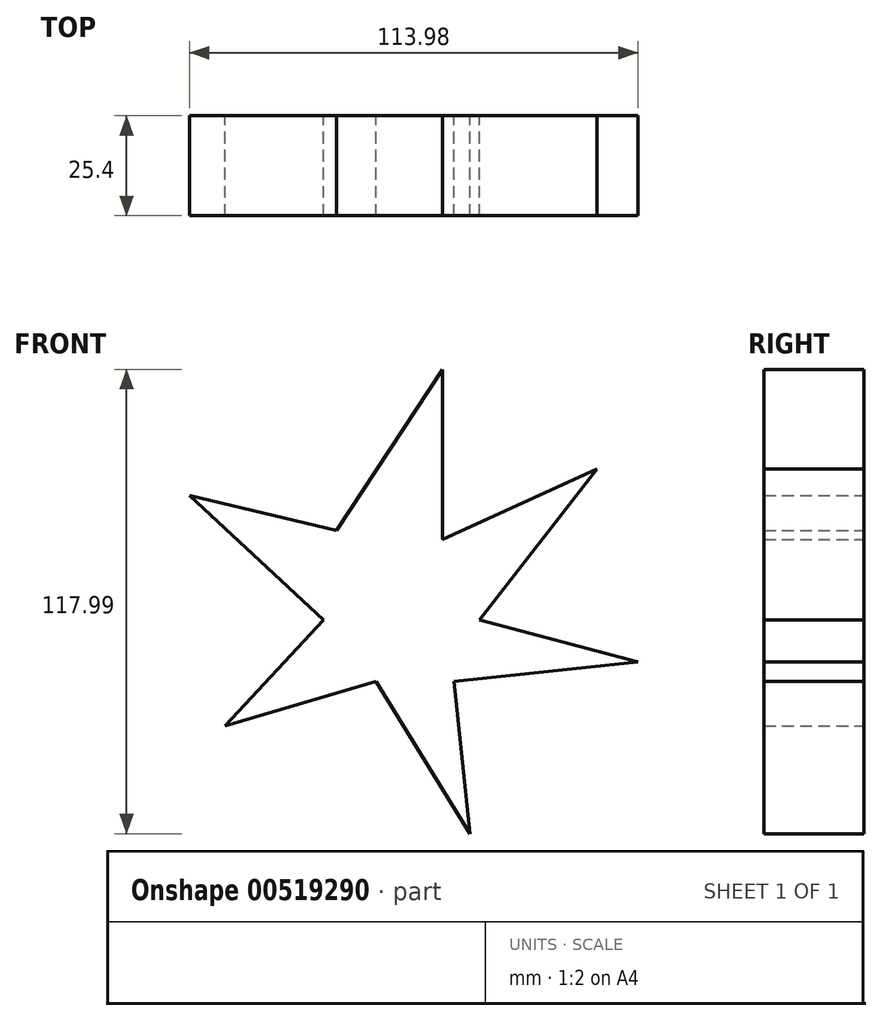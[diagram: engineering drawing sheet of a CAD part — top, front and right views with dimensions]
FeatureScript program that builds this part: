
annotation { "Feature Type Name" : "Feature", "Feature Type Description" : "" }
export const myFeature = defineFeature(function(context is Context, id is Id, definition is map)
    precondition{}
    {
        {
            var Q0;
            Q0=qCreatedBy(makeId("Front.planeOp"),FACE);
            var sketch = newSketch(context, id + "F0", { "sketchPlane" : qUnion([Q0])});
            skLineSegment(sketch, "E0", {"start": v(-33.92, 20.42) * mm, "end": v(-6.96, 61.36) * mm});
            skLineSegment(sketch, "E1", {"start": v(-6.96, 61.36) * mm, "end": v(-6.96, 18.15) * mm});
            skLineSegment(sketch, "E2", {"start": v(-6.96, 18.15) * mm, "end": v(32.35, 36.02) * mm});
            skLineSegment(sketch, "E3", {"start": v(32.35, 36.02) * mm, "end": v(2.46, -2.32) * mm});
            skLineSegment(sketch, "E4", {"start": v(2.46, -2.32) * mm, "end": v(42.75, -13.04) * mm});
            skLineSegment(sketch, "E5", {"start": v(42.75, -13.04) * mm, "end": v(-4.03, -17.91) * mm});
            skLineSegment(sketch, "E6", {"start": v(-4.03, -17.91) * mm, "end": v(0, -56.63) * mm});
            skLineSegment(sketch, "E7", {"start": v(0, -56.63) * mm, "end": v(-23.85, -17.91) * mm});
            skLineSegment(sketch, "E8", {"start": v(-23.85, -17.91) * mm, "end": v(-62.19, -29.28) * mm});
            skLineSegment(sketch, "E9", {"start": v(-62.19, -29.28) * mm, "end": v(-37.17, -2.32) * mm});
            skLineSegment(sketch, "E10", {"start": v(-37.17, -2.32) * mm, "end": v(-71.23, 29.28) * mm});
            skLineSegment(sketch, "E11", {"start": v(-71.23, 29.28) * mm, "end": v(-33.92, 20.42) * mm});
            skSolve(sketch);
        }
        {
            var Q0;
            Q0=makeQuery(id+"F0.imprint","IMPRINT",FACE,{"disambiguationData":[TD([[makeQuery(id+"F0.imprint","IMPRINT",EDGE,{"derivedFrom":sQuery(id+"F0.wireOp",EDGE,"E0")}),-1.0]])]});
            extrude(context, id + "F1", {"entities" : qUnion([Q0]), "depth" : 25.4 * mm, "offsetDistance" : 25.4 * mm});
        }
        {
            var Q0;
            Q0 = qConstructionFilter(qBodyType(qCreatedBy(id + "F0" ,EDGE), BodyType.WIRE), ConstructionObject.NO);
            extrude(context, id + "F2", {"bodyType" : ToolBodyType.SURFACE, "surfaceEntities" : qUnion([Q0]), "depth" : 25.4 * mm, "offsetDistance" : 25.4 * mm});
        }
    });
